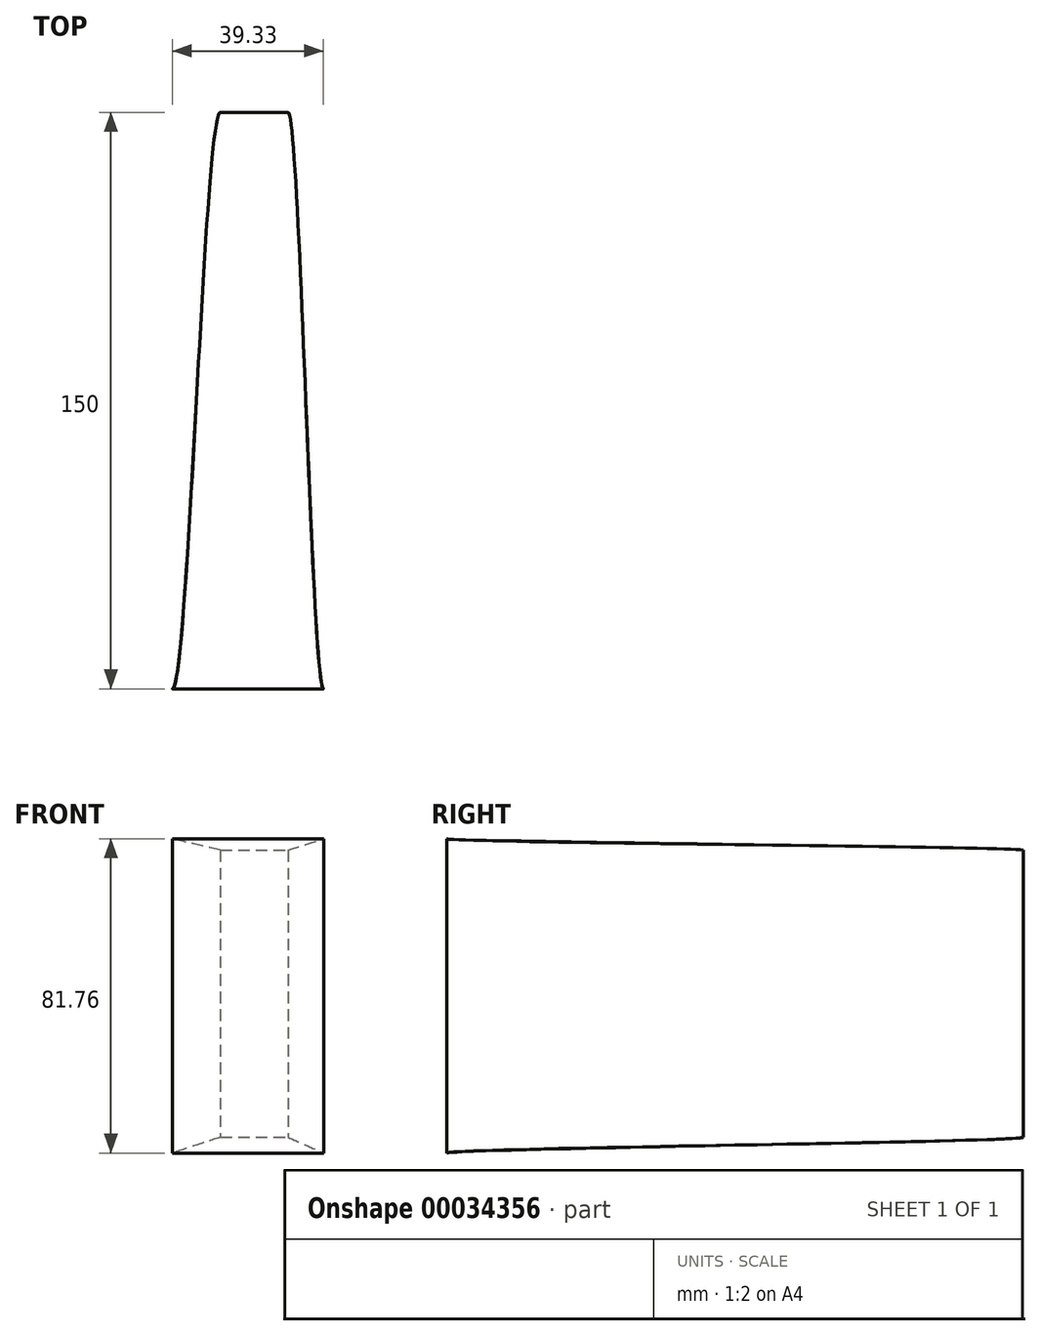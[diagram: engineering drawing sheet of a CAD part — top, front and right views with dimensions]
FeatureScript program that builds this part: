
annotation { "Feature Type Name" : "Feature", "Feature Type Description" : "" }
export const myFeature = defineFeature(function(context is Context, id is Id, definition is map)
    precondition{}
    {
        {
            var Q0;
            Q0=qCreatedBy(makeId("Front.planeOp"),FACE);
            var sketch = newSketch(context, id + "F0", { "sketchPlane" : qUnion([Q0])});
            skLineSegment(sketch, "E0.bottom", {"start": v(-8.45, 42.07) * mm, "end": v(9.15, 42.07) * mm});
            skLineSegment(sketch, "E0.top", {"start": v(-8.45, -32.57) * mm, "end": v(9.15, -32.57) * mm});
            skLineSegment(sketch, "E0.left", {"start": v(-8.45, 42.07) * mm, "end": v(-8.45, -32.57) * mm});
            skLineSegment(sketch, "E0.right", {"start": v(9.15, 42.07) * mm, "end": v(9.15, -32.57) * mm});
            skSolve(sketch);
        }
        {
            var Q0;
            Q0=qCreatedBy(makeId("Front.planeOp"),FACE);
            cPlane(context, id + "F1", {"entities" : qUnion([Q0]), "cplaneType" : CPlaneType.OFFSET, "offset" : 150 * mm, "width" : 150 * mm, "height" : 150 * mm});
        }
        {
            var Q0;
            Q0=qCreatedBy(id+"F1.planeOp",FACE);
            var sketch = newSketch(context, id + "F2", { "sketchPlane" : qUnion([Q0])});
            skLineSegment(sketch, "E1.bottom", {"start": v(18.38, 45.07) * mm, "end": v(-20.95, 45.07) * mm});
            skLineSegment(sketch, "E1.top", {"start": v(18.38, -36.69) * mm, "end": v(-20.95, -36.69) * mm});
            skLineSegment(sketch, "E1.left", {"start": v(18.38, 45.07) * mm, "end": v(18.38, -36.69) * mm});
            skLineSegment(sketch, "E1.right", {"start": v(-20.95, 45.07) * mm, "end": v(-20.95, -36.69) * mm});
            skSolve(sketch);
        }
        {
            var Q0;
            Q0=qCreatedBy(makeId("Right.planeOp"),FACE);
            var sketch = newSketch(context, id + "F3", { "sketchPlane" : qUnion([Q0])});
            skLineSegment(sketch, "E2.0", {"start": v(-150, 45.07) * mm, "end": v(-150, -36.69) * mm});
            skLineSegment(sketch, "E3.1", {"start": v(0, 42.07) * mm, "end": v(0, -32.57) * mm});
            skFitSpline(sketch, "E4", {"points": [v(0, -32.57) * mm, v(-24.1, -43.94) * mm, v(-67.33, -36.83) * mm, v(-107, -16.11) * mm, v(-124.17, -32.57) * mm, v(-150, -36.69) * mm], "startDerivative": vector(-120.69, -76.97) * mm, "endDerivative": vector(-160.06, 48.5) * mm});
            skFitSpline(sketch, "E5", {"points": [v(0, 42.07) * mm, v(-69.7, 18.23) * mm, v(-150, 45.07) * mm], "startDerivative": vector(-141.82, -73.83) * mm, "endDerivative": vector(-157.99, 78.06) * mm});
            skSolve(sketch);
        }
        {
            var Q0;
            Q0=makeQuery(id+"F0.imprint","IMPRINT",FACE,{"disambiguationData":[TD([[makeQuery(id+"F0.imprint","IMPRINT",EDGE,{"derivedFrom":sQuery(id+"F0.wireOp",EDGE,"E0.bottom")}),-1.0]])]});
            var Q1;
            Q1=makeQuery(id+"F2.imprint","IMPRINT",FACE,{"disambiguationData":[TD([[makeQuery(id+"F2.imprint","IMPRINT",EDGE,{"derivedFrom":sQuery(id+"F2.wireOp",EDGE,"E1.bottom")}),1.0]])]});
            var Q2;
            Q2=sQuery(id+"F3.wireOp",EDGE,"E4");
            var Q3;
            Q3=sQuery(id+"F3.wireOp",EDGE,"E5");
            var Q4;
            Q4=sQuery(id+"F0.wireOp",VERTEX,"E0.right.end");
            var Q5;
            Q5=sQuery(id+"F2.wireOp",VERTEX,"E1.left.end");
            loft(context, id + "F4", {"startCondition" : LoftEndDerivativeType.TANGENT_TO_PROFILE, "startMagnitude" : 1, "endCondition" : LoftEndDerivativeType.TANGENT_TO_PROFILE, "endMagnitude" : 1, "sheetProfilesArray" : [{ "sheetProfileEntities" : qUnion([Q0]) }, { "sheetProfileEntities" : qUnion([Q1]) }], "guidesArray" : [{ "guideEntities" : qUnion([Q2]), "guideDerivativeType" : LoftGuideDerivativeType.DEFAULT, "guideDerivativeMagnitude" : 1 }, { "guideEntities" : qUnion([Q3]), "guideDerivativeType" : LoftGuideDerivativeType.DEFAULT, "guideDerivativeMagnitude" : 1 }], "connections" : [{ "connectionEntities" : qUnion([Q4, Q5]), "connectionEdgeQueries" : qUnion([]), "connectionEdgeParameters" : [] }]});
        }
    });
